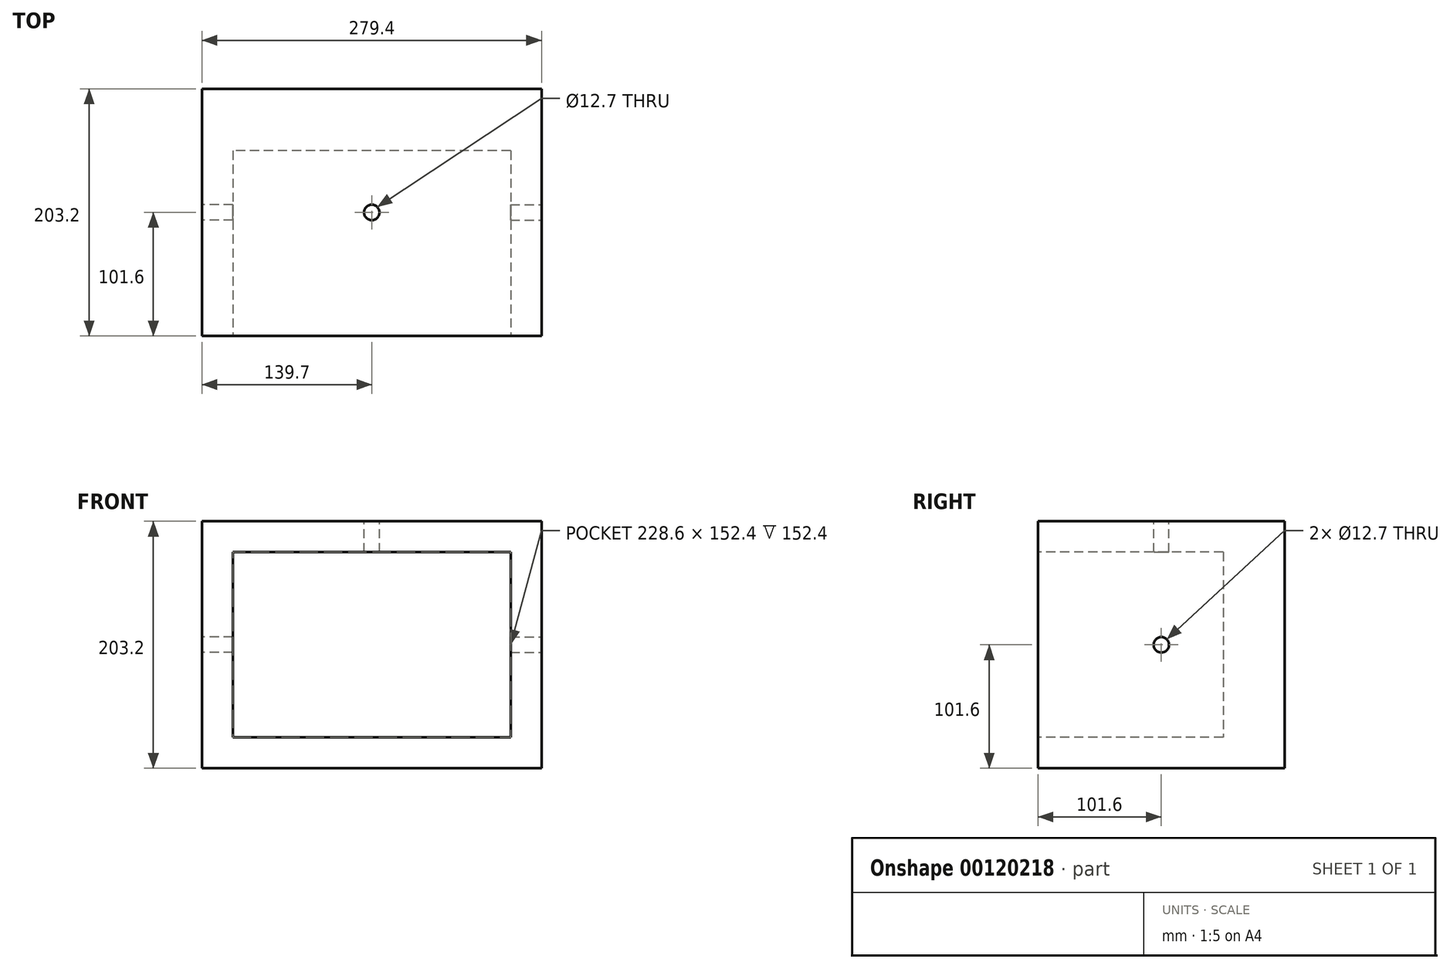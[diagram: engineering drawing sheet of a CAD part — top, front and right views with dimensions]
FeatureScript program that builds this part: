
annotation { "Feature Type Name" : "Feature", "Feature Type Description" : "" }
export const myFeature = defineFeature(function(context is Context, id is Id, definition is map)
    precondition{}
    {
        {
            var Q0;
            Q0=qCreatedBy(makeId("Front.planeOp"),FACE);
            var sketch = newSketch(context, id + "F0", { "sketchPlane" : qUnion([Q0])});
            skLineSegment(sketch, "E0.bottom", {"start": v(-139.7, 101.6) * mm, "end": v(139.7, 101.6) * mm});
            skLineSegment(sketch, "E0.top", {"start": v(-139.7, -101.6) * mm, "end": v(139.7, -101.6) * mm});
            skLineSegment(sketch, "E0.left", {"start": v(-139.7, 101.6) * mm, "end": v(-139.7, -101.6) * mm});
            skLineSegment(sketch, "E0.right", {"start": v(139.7, 101.6) * mm, "end": v(139.7, -101.6) * mm});
            skPoint(sketch, "E0.middle", {"position": v(0, 0) * mm});
            skSolve(sketch);
        }
        {
            var Q0;
            Q0=makeQuery(id+"F0.imprint","IMPRINT",FACE,{"disambiguationData":[TD([[makeQuery(id+"F0.imprint","IMPRINT",EDGE,{"derivedFrom":sQuery(id+"F0.wireOp",EDGE,"E0.bottom")}),-1.0]])]});
            extrude(context, id + "F1", {"entities" : qUnion([Q0]), "oppositeDirection" : true, "depth" : 203.2 * mm});
        }
        {
            var Q0;
            Q0=makeQuery(id+"F1.opExtrude","SWEPT_FACE",FACE,{"disambiguationData":[OSD([sQuery(id+"F0.wireOp",EDGE,"E0.bottom")])]});
            var sketch = newSketch(context, id + "F2", { "sketchPlane" : qUnion([Q0])});
            skCircle(sketch, "E1", {"center": v(0, 101.6) * mm, "radius": 6.35 * mm});
            skPoint(sketch, "E1.centerSnap0", {"position": v(139.7, 101.6) * mm});
            skSolve(sketch);
        }
        {
            var Q0;
            Q0=makeQuery(id+"F1.opExtrude","SWEPT_FACE",FACE,{"disambiguationData":[OSD([sQuery(id+"F0.wireOp",EDGE,"E0.right")])]});
            var sketch = newSketch(context, id + "F3", { "sketchPlane" : qUnion([Q0])});
            skCircle(sketch, "E2", {"center": v(101.6, 0) * mm, "radius": 6.35 * mm});
            skPoint(sketch, "E2.centerSnap0", {"position": v(101.6, -101.6) * mm});
            skSolve(sketch);
        }
        {
            var Q0;
            Q0=makeQuery(id+"F1.opExtrude","SWEPT_FACE",FACE,{"disambiguationData":[OSD([sQuery(id+"F0.wireOp",EDGE,"E0.left")])]});
            var sketch = newSketch(context, id + "F4", { "sketchPlane" : qUnion([Q0])});
            skCircle(sketch, "E3", {"center": v(-101.6, 0) * mm, "radius": 6.35 * mm});
            skPoint(sketch, "E3.centerSnap0", {"position": v(-101.6, 101.6) * mm});
            skSolve(sketch);
        }
        {
            var Q0;
            Q0=qCreatedBy(makeId("Front.planeOp"),FACE);
            var sketch = newSketch(context, id + "F5", { "sketchPlane" : qUnion([Q0])});
            skLineSegment(sketch, "E4.bottom", {"start": v(114.3, 76.2) * mm, "end": v(-114.3, 76.2) * mm});
            skLineSegment(sketch, "E4.top", {"start": v(114.3, -76.2) * mm, "end": v(-114.3, -76.2) * mm});
            skLineSegment(sketch, "E4.left", {"start": v(114.3, 76.2) * mm, "end": v(114.3, -76.2) * mm});
            skLineSegment(sketch, "E4.right", {"start": v(-114.3, 76.2) * mm, "end": v(-114.3, -76.2) * mm});
            skSolve(sketch);
        }
        {
            var Q0;
            Q0 = qSketchRegion(id + "F5", true);
            extrude(context, id + "F6", {"entities" : qUnion([Q0]), "operationType" : NewBodyOperationType.REMOVE, "oppositeDirection" : true, "depth" : 152.4 * mm});
        }
        {
            var Q0;
            Q0=makeQuery(id+"F2.imprint","IMPRINT",FACE,{"disambiguationData":[TD([[makeQuery(id+"F2.imprint","IMPRINT",EDGE,{"derivedFrom":sQuery(id+"F2.wireOp",EDGE,"E1")}),1.0]])]});
            var Q1;
            Q1=sQuery(id+"F2.wireOp",EDGE,"E1");
            extrude(context, id + "F7", {"entities" : qUnion([Q0]), "operationType" : NewBodyOperationType.REMOVE, "surfaceEntities" : qUnion([Q1]), "oppositeDirection" : true, "depth" : 25.4 * mm});
        }
        {
            var Q0;
            Q0 = qSketchRegion(id + "F3", true);
            extrude(context, id + "F8", {"entities" : qUnion([Q0]), "operationType" : NewBodyOperationType.REMOVE, "oppositeDirection" : true, "depth" : 25.4 * mm});
        }
        {
            var Q0;
            Q0 = qSketchRegion(id + "F4", true);
            extrude(context, id + "F9", {"entities" : qUnion([Q0]), "operationType" : NewBodyOperationType.REMOVE, "oppositeDirection" : true, "depth" : 25.4 * mm});
        }
    });
